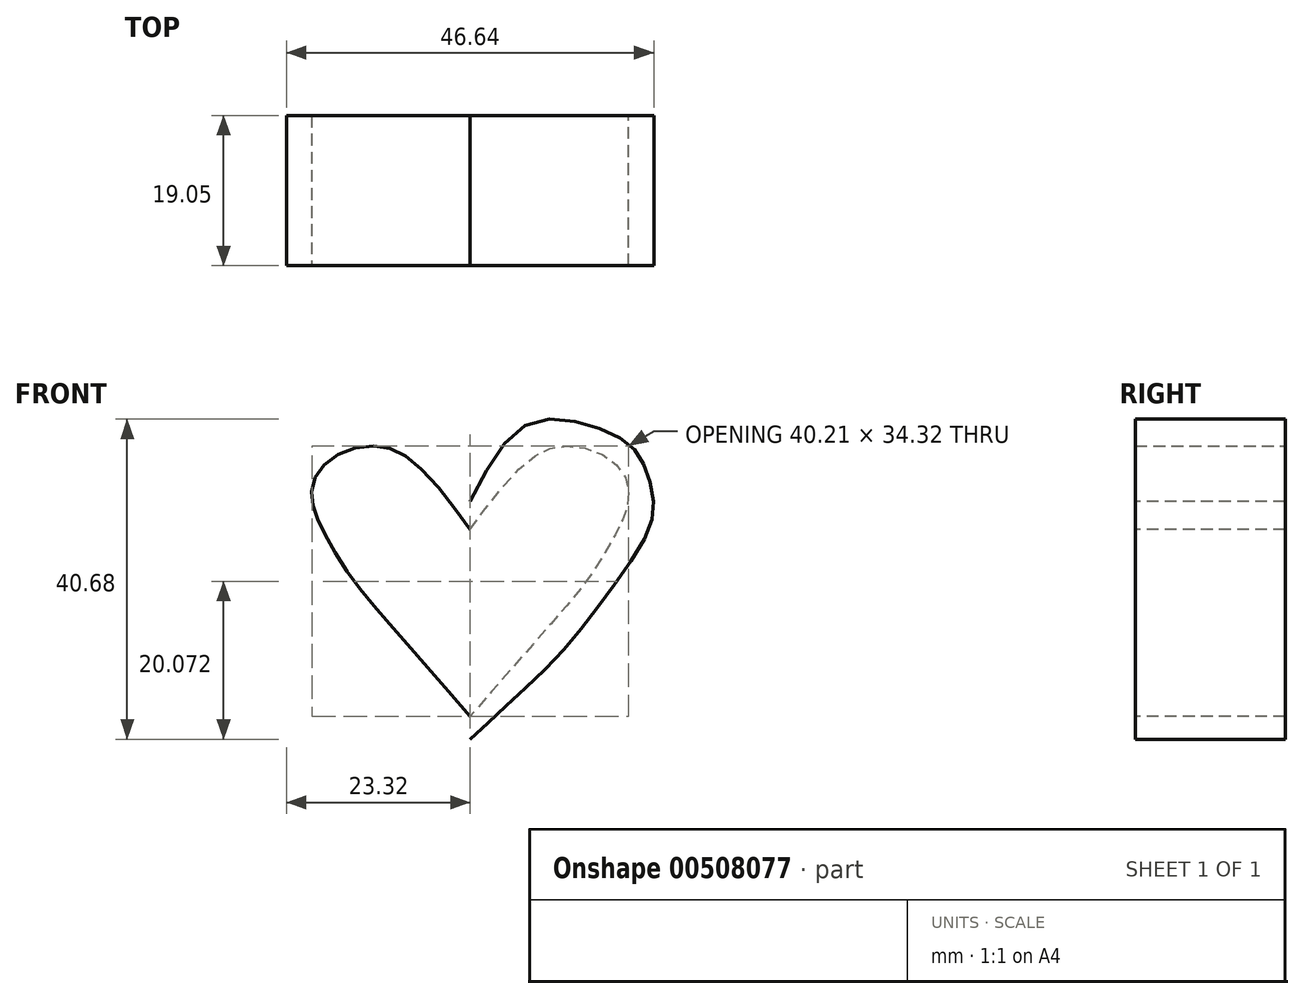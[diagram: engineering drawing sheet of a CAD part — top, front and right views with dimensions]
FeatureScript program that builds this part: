
annotation { "Feature Type Name" : "Feature", "Feature Type Description" : "" }
export const myFeature = defineFeature(function(context is Context, id is Id, definition is map)
    precondition{}
    {
        {
            var Q0;
            Q0=qCreatedBy(makeId("Front.planeOp"),FACE);
            var sketch = newSketch(context, id + "F0", { "sketchPlane" : qUnion([Q0])});
            skFitSpline(sketch, "E0", {"points": [v(0, 0) * mm, v(6.95, 9.63) * mm, v(14.55, 9.86) * mm, v(20.08, 7.33) * mm, v(22.15, 4.45) * mm, v(23.3, 0) * mm, v(22.38, -4.3) * mm, v(17.31, -11.9) * mm, v(11.78, -18.93) * mm, v(5.45, -25.15) * mm, v(0, -30.21) * mm], "startDerivative": vector(47.19, 93.17) * mm, "endDerivative": vector(-51.53, -48) * mm});
            skFitSpline(sketch, "E1.MirrorCS", {"points": [v(0, 0) * mm, v(-6.95, 9.63) * mm, v(-14.55, 9.86) * mm, v(-20.08, 7.33) * mm, v(-22.15, 4.45) * mm, v(-23.3, 0) * mm, v(-22.38, -4.3) * mm, v(-17.31, -11.9) * mm, v(-11.78, -18.93) * mm, v(-5.45, -25.15) * mm, v(0, -30.21) * mm], "startDerivative": vector(-47.19, 93.17) * mm, "endDerivative": vector(51.53, -48) * mm});
            skSolve(sketch);
        }
        {
            var Q0;
            Q0=qSketchRegion(id+"F0",true);
            extrude(context, id + "F1", {"entities" : qUnion([Q0]), "oppositeDirection" : true, "depth" : 19.05 * mm});
        }
        {
            var Q0;
            Q0=qCreatedBy(makeId("Front.planeOp"),FACE);
            var sketch = newSketch(context, id + "F2", { "sketchPlane" : qUnion([Q0])});
            skFitSpline(sketch, "E2", {"points": [v(0, -3.56) * mm, v(6.76, 4.62) * mm, v(11.2, 6.97) * mm, v(16.33, 6.18) * mm, v(19.63, 3.23) * mm, v(20.07, 0) * mm, v(18.94, -3.2) * mm, v(15.28, -9.38) * mm, v(10.07, -15.73) * mm, v(0, -27.3) * mm], "startDerivative": vector(39.07, 56.91) * mm, "endDerivative": vector(-62.75, -72.4) * mm});
            skFitSpline(sketch, "E3.MirrorCS", {"points": [v(0, -3.56) * mm, v(-6.76, 4.62) * mm, v(-11.2, 6.97) * mm, v(-16.33, 6.18) * mm, v(-19.63, 3.23) * mm, v(-20.07, 0) * mm, v(-18.94, -3.2) * mm, v(-15.28, -9.38) * mm, v(-10.07, -15.73) * mm, v(0, -27.3) * mm], "startDerivative": vector(-39.07, 56.91) * mm, "endDerivative": vector(62.75, -72.4) * mm});
            skSolve(sketch);
        }
        {
            var Q0;
            Q0=qSketchRegion(id+"F2",true);
            extrude(context, id + "F3", {"entities" : qUnion([Q0]), "operationType" : NewBodyOperationType.REMOVE, "oppositeDirection" : true, "depth" : 19.05 * mm});
        }
    });
